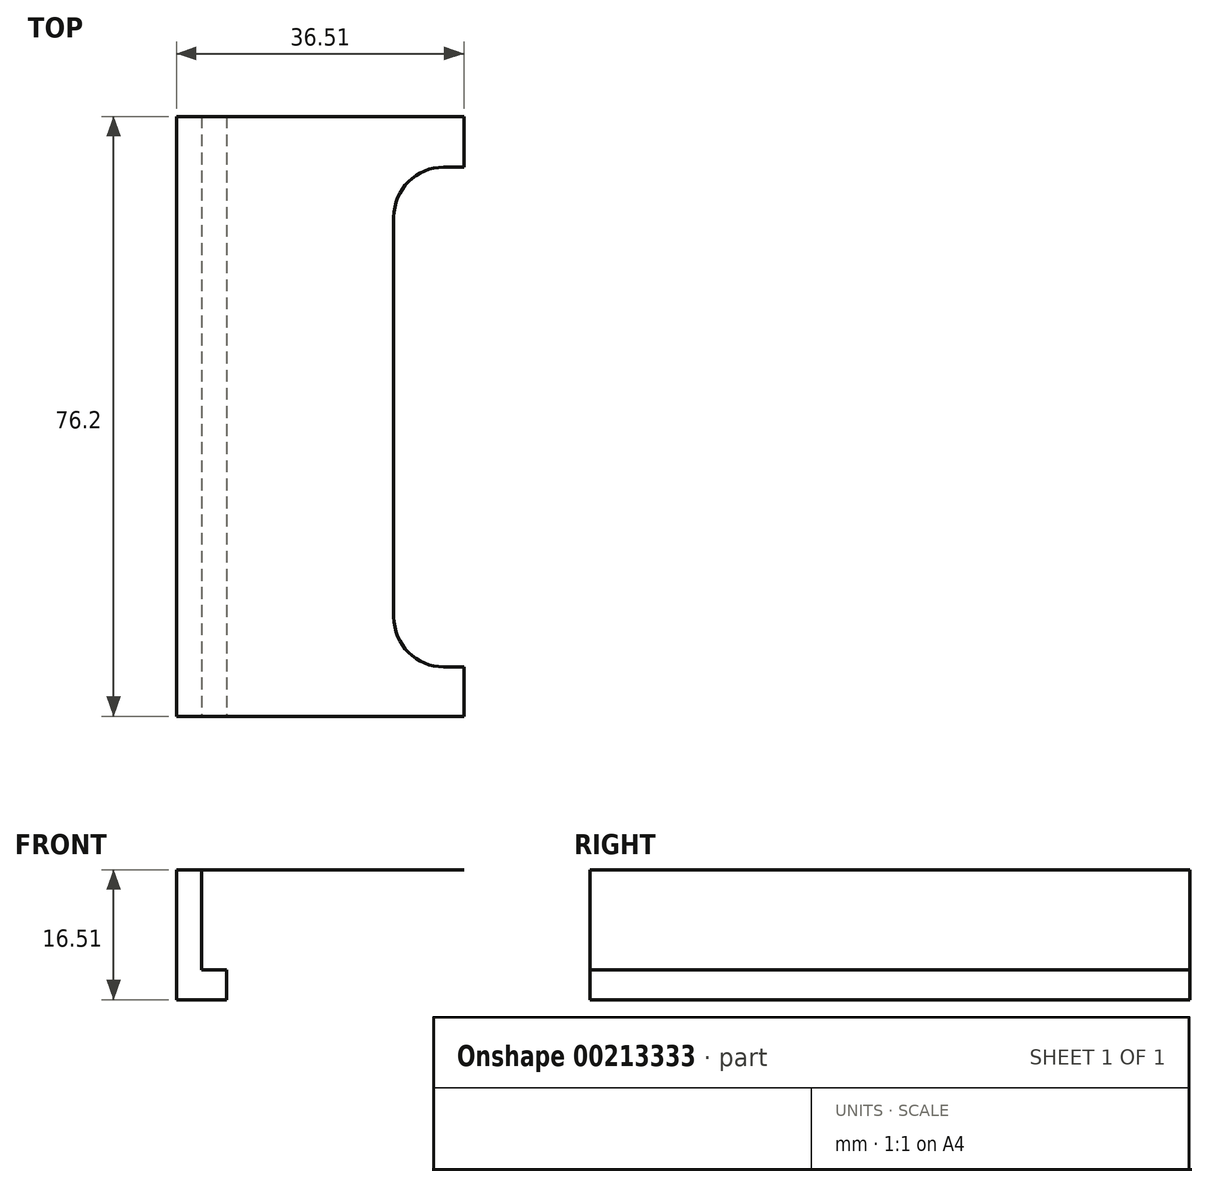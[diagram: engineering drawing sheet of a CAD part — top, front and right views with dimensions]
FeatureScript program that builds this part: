
annotation { "Feature Type Name" : "Feature", "Feature Type Description" : "" }
export const myFeature = defineFeature(function(context is Context, id is Id, definition is map)
    precondition{}
    {
        {
            var Q0;
            Q0=qCreatedBy(makeId("Top.planeOp"),FACE);
            var sketch = newSketch(context, id + "F0", { "sketchPlane" : qUnion([Q0])});
            skLineSegment(sketch, "E0.bottom", {"start": v(-36.51, -38.1) * mm, "end": v(0, -38.1) * mm});
            skLineSegment(sketch, "E0.top", {"start": v(-36.51, 38.1) * mm, "end": v(0, 38.1) * mm});
            skLineSegment(sketch, "E0.left", {"start": v(-36.51, -38.1) * mm, "end": v(-36.51, 38.1) * mm});
            skPoint(sketch, "E0.middle", {"position": v(0, 0) * mm});
            skLineSegment(sketch, "E1", {"start": v(-33.34, 38.1) * mm, "end": v(-33.34, -38.1) * mm});
            skLineSegment(sketch, "E2", {"start": v(-30.16, 38.1) * mm, "end": v(-30.16, -38.1) * mm});
            skLineSegment(sketch, "E3", {"start": v(0, 38.1) * mm, "end": v(0, -38.1) * mm});
            skPoint(sketch, "E4.orphan", {"position": v(36.51, 38.1) * mm});
            skPoint(sketch, "E5.orphan", {"position": v(36.51, -38.1) * mm});
            skLineSegment(sketch, "E6", {"start": v(-8.9, -25.5) * mm, "end": v(-8.9, 25.3) * mm});
            skLineSegment(sketch, "E7", {"start": v(-2.55, -31.85) * mm, "end": v(0, -31.85) * mm});
            skPoint(sketch, "E8.visualSharp", {"position": v(-8.9, -31.85) * mm});
            skArc(sketch, "E8.filletArc", {"start": v(-8.9, -25.5) * mm, "mid": v(-7.04, -29.99) * mm, "end": v(-2.55, -31.85) * mm});
            skLineSegment(sketch, "E9", {"start": v(-2.55, 31.65) * mm, "end": v(0, 31.65) * mm});
            skPoint(sketch, "E10.visualSharp", {"position": v(-8.9, 31.65) * mm});
            skArc(sketch, "E10.filletArc", {"start": v(-2.55, 31.65) * mm, "mid": v(-7.04, 29.8) * mm, "end": v(-8.9, 25.3) * mm});
            skSolve(sketch);
        }
        {
            var Q0;
            {var subQ0=sQuery(id+"F0.wireOp",EDGE,"E0.left");Q0=makeQuery(id+"F0.imprint","IMPRINT",FACE,{"disambiguationData":[TD([[makeQuery(id+"F0.imprint","IMPRINT",EDGE,{"derivedFrom":subQ0}),-1.0]])]});}
            var Q1;
            {var subQ2=sQuery(id+"F0.wireOp",EDGE,"E2");Q1=makeQuery(id+"F0.imprint","IMPRINT",FACE,{"disambiguationData":[TD([[makeQuery(id+"F0.imprint","IMPRINT",EDGE,{"derivedFrom":subQ2}),1.0]])]});}
            var Q2;
            {var subQ0=sQuery(id+"F0.wireOp",EDGE,"E1");Q2=makeQuery(id+"F0.imprint","IMPRINT",FACE,{"disambiguationData":[TD([[makeQuery(id+"F0.imprint","IMPRINT",EDGE,{"derivedFrom":subQ0}),1.0]])]});}
            extrude(context, id + "F1", {"entities" : qUnion([Q0, Q1, Q2]), "depth" : 3 / 1625.6 * mm});
        }
        {
            var Q0;
            {var subQ0=sQuery(id+"F0.wireOp",EDGE,"E0.left");Q0=makeQuery(id+"F0.imprint","IMPRINT",FACE,{"disambiguationData":[TD([[makeQuery(id+"F0.imprint","IMPRINT",EDGE,{"derivedFrom":subQ0}),-1.0]])]});}
            extrude(context, id + "F2", {"entities" : qUnion([Q0]), "operationType" : NewBodyOperationType.ADD, "oppositeDirection" : true, "depth" : 16.5 * mm});
        }
        {
            var Q0;
            {var subQ0=sQuery(id+"F0.wireOp",EDGE,"E0.left");Q0=makeQuery(id+"F0.imprint","IMPRINT",FACE,{"disambiguationData":[TD([[makeQuery(id+"F0.imprint","IMPRINT",EDGE,{"derivedFrom":subQ0}),-1.0]])]});}
            var Q1;
            {var subQ0=sQuery(id+"F0.wireOp",EDGE,"E1");Q1=makeQuery(id+"F0.imprint","IMPRINT",FACE,{"disambiguationData":[TD([[makeQuery(id+"F0.imprint","IMPRINT",EDGE,{"derivedFrom":subQ0}),1.0]])]});}
            extrude(context, id + "F3", {"entities" : qUnion([Q0, Q1]), "operationType" : NewBodyOperationType.ADD, "oppositeDirection" : true, "depth" : 16.5 * mm, "hasSecondDirection" : true, "secondDirectionOppositeDirection" : true, "secondDirectionDepth" : 12.7 * mm});
        }
    });
